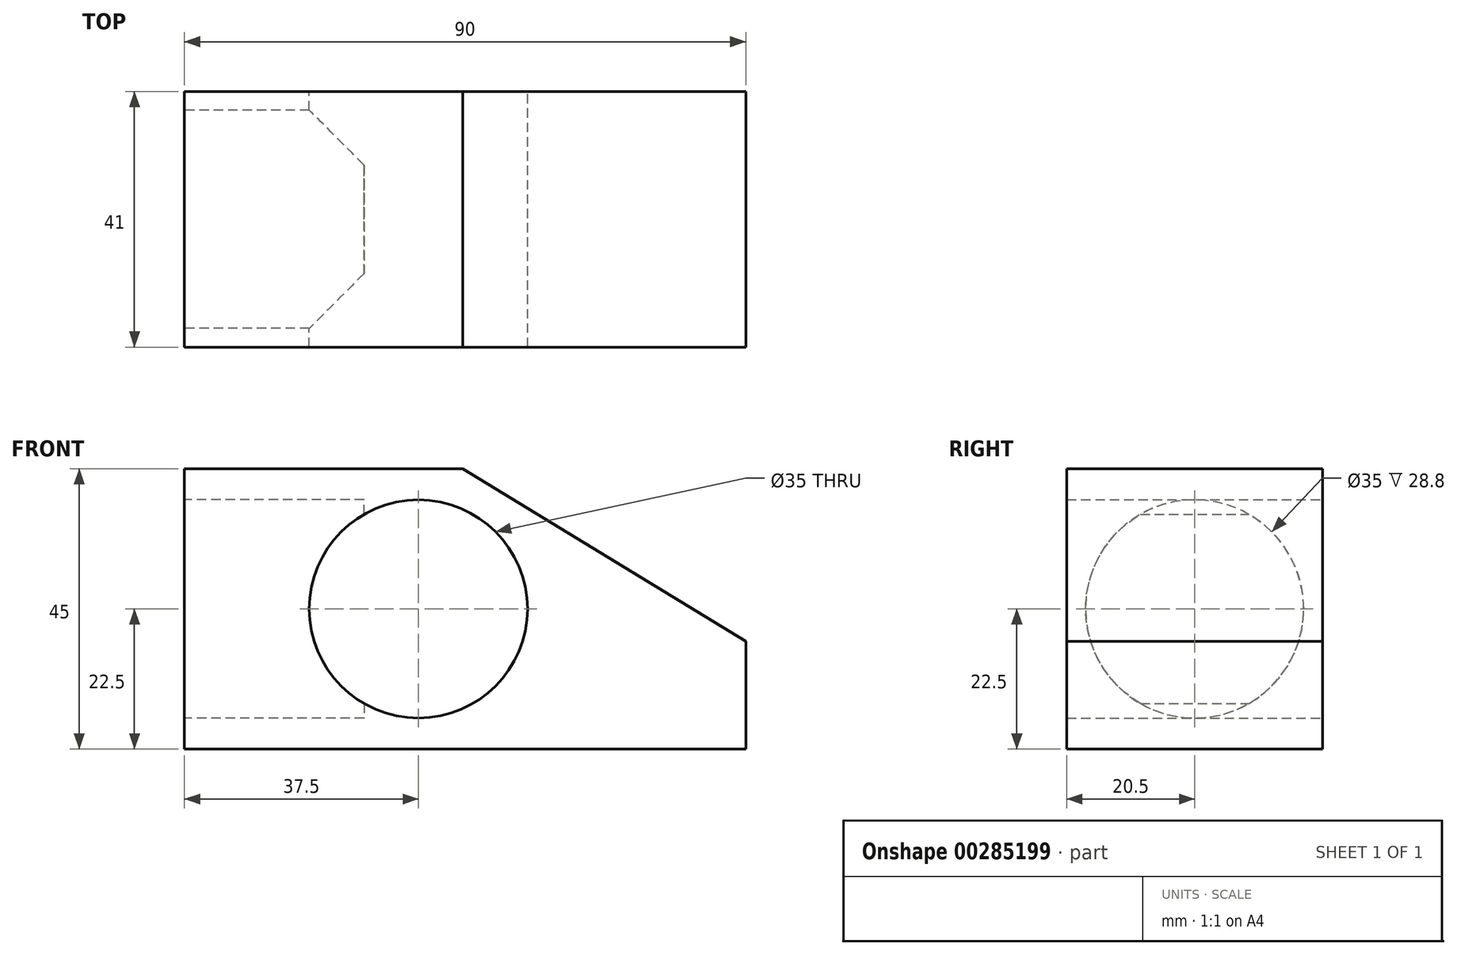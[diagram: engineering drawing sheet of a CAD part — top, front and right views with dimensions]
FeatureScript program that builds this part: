
annotation { "Feature Type Name" : "Feature", "Feature Type Description" : "" }
export const myFeature = defineFeature(function(context is Context, id is Id, definition is map)
    precondition{}
    {
        {
            var Q0;
            Q0=qCreatedBy(makeId("Front.planeOp"),FACE);
            var sketch = newSketch(context, id + "F0", { "sketchPlane" : qUnion([Q0])});
            skLineSegment(sketch, "E0.bottom", {"start": v(-45, 22.5) * mm, "end": v(45, 22.5) * mm});
            skLineSegment(sketch, "E0.top", {"start": v(-45, -22.5) * mm, "end": v(45, -22.5) * mm});
            skLineSegment(sketch, "E0.left", {"start": v(-45, 22.5) * mm, "end": v(-45, -22.5) * mm});
            skLineSegment(sketch, "E0.right", {"start": v(45, 22.5) * mm, "end": v(45, -22.5) * mm});
            skPoint(sketch, "E0.middle", {"position": v(0, 0) * mm});
            skSolve(sketch);
        }
        {
            var Q0;
            Q0 = qSketchRegion(id + "F0", true);
            extrude(context, id + "F1", {"entities" : qUnion([Q0]), "depth" : 41 * mm});
        }
        {
            var Q0;
            Q0=qCreatedBy(makeId("Front.planeOp"),FACE);
            var sketch = newSketch(context, id + "F2", { "sketchPlane" : qUnion([Q0])});
            skCircle(sketch, "E1", {"center": v(-7.5, 0) * mm, "radius": 17.5 * mm});
            skSolve(sketch);
        }
        {
            var Q0;
            Q0 = qSketchRegion(id + "F2", true);
            extrude(context, id + "F3", {"entities" : qUnion([Q0]), "operationType" : NewBodyOperationType.REMOVE, "depth" : 80.04 * mm});
        }
        {
            var Q0;
            Q0=makeQuery(id+"F0.imprint","IMPRINT",FACE,{"disambiguationData":[TD([[makeQuery(id+"F0.imprint","IMPRINT",EDGE,{"derivedFrom":sQuery(id+"F0.wireOp",EDGE,"E0.bottom")}),-1.0]])]});
            var sketch = newSketch(context, id + "F4", { "sketchPlane" : qUnion([Q0])});
            skLineSegment(sketch, "E2", {"start": v(50.25, -8.43) * mm, "end": v(-20.4, 34.71) * mm});
            skLineSegment(sketch, "E3", {"start": v(-20.4, 34.71) * mm, "end": v(50.31, 38.42) * mm});
            skLineSegment(sketch, "E4", {"start": v(50.31, 38.42) * mm, "end": v(50.25, -8.43) * mm});
            skSolve(sketch);
        }
        {
            var Q0;
            Q0 = qSketchRegion(id + "F4", true);
            extrude(context, id + "F5", {"entities" : qUnion([Q0]), "operationType" : NewBodyOperationType.REMOVE, "endBound" : BoundingType.SYMMETRIC, "depth" : 120 * mm});
        }
        {
            var Q0;
            Q0=makeQuery(id+"F1.opExtrude","SWEPT_FACE",FACE,{"disambiguationData":[OSD([sQuery(id+"F0.wireOp",EDGE,"E0.left")])]});
            var sketch = newSketch(context, id + "F6", { "sketchPlane" : qUnion([Q0])});
            skLineSegment(sketch, "E5", {"start": v(0, 22.5) * mm, "end": v(41, -22.5) * mm, "construction": true});
            skLineSegment(sketch, "E6", {"start": v(41, -22.5) * mm, "end": v(41, 22.5) * mm, "construction": true});
            skLineSegment(sketch, "E7", {"start": v(41, 22.5) * mm, "end": v(0, -22.5) * mm, "construction": true});
            skCircle(sketch, "E8", {"center": v(20.5, 0) * mm, "radius": 17.5 * mm});
            skSolve(sketch);
        }
        {
            var Q0;
            Q0 = qSketchRegion(id + "F6", true);
            extrude(context, id + "F7", {"entities" : qUnion([Q0]), "operationType" : NewBodyOperationType.REMOVE, "oppositeDirection" : true, "depth" : 28.8 * mm, "offsetDistance" : 25 * mm});
        }
    });
